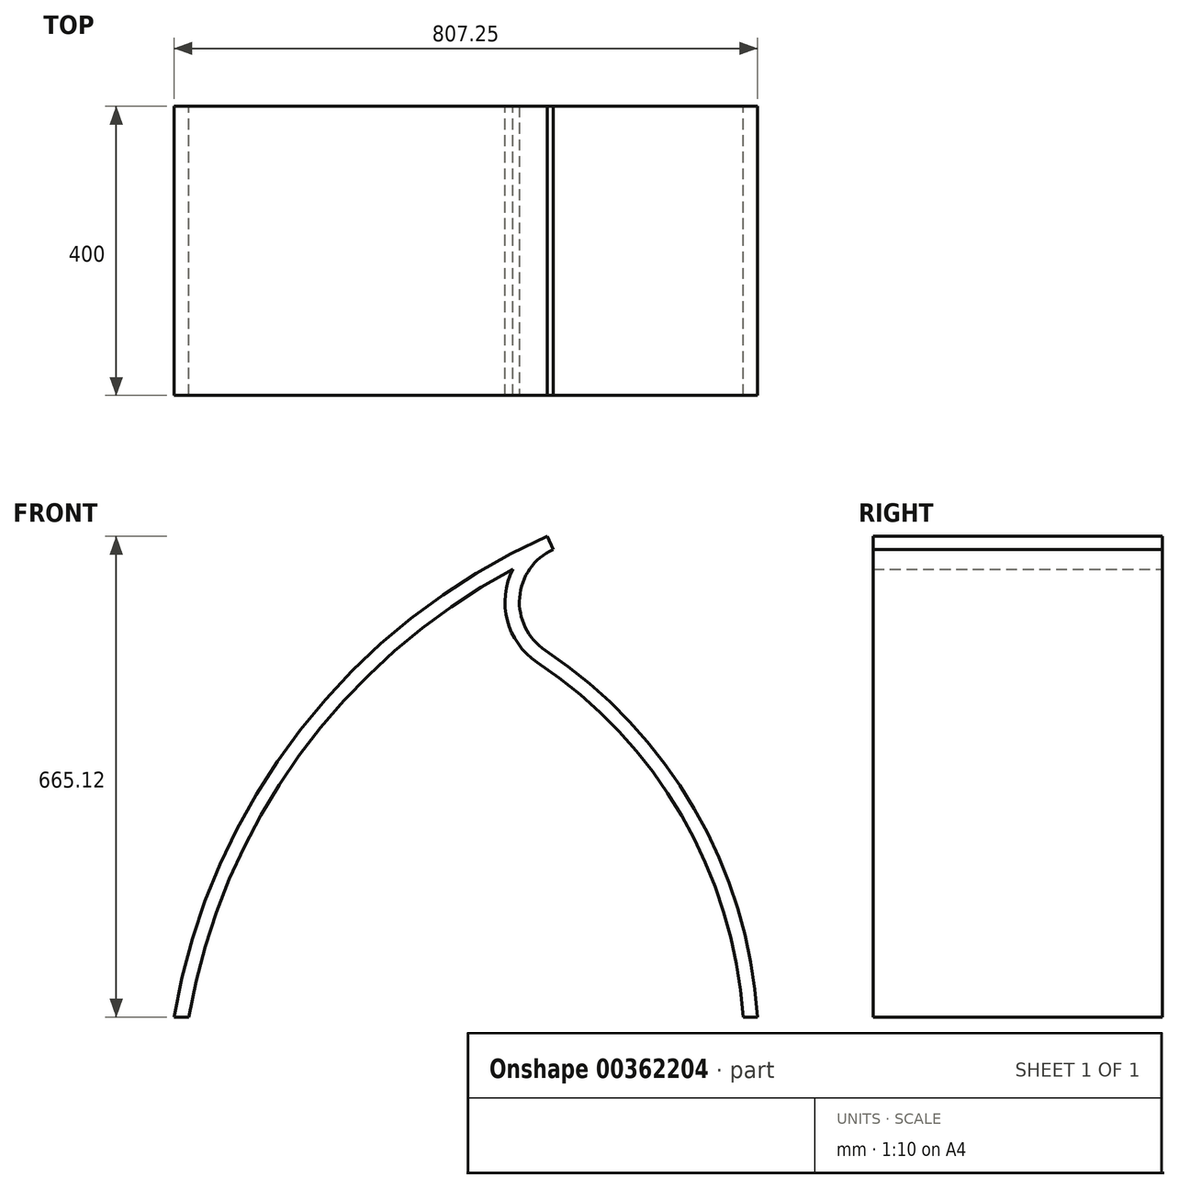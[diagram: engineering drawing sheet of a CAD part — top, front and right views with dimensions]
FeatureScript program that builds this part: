
annotation { "Feature Type Name" : "Feature", "Feature Type Description" : "" }
export const myFeature = defineFeature(function(context is Context, id is Id, definition is map)
    precondition{}
    {
        {
            var Q0;
            Q0=qCreatedBy(makeId("Front.planeOp"),FACE);
            var sketch = newSketch(context, id + "F0", { "sketchPlane" : qUnion([Q0])});
            skArc(sketch, "E0", {"start": v(516.46, 665.12) * mm, "mid": v(174.8, 397.34) * mm, "end": v(0, 0) * mm});
            skArc(sketch, "E1.0", {"start": v(524.6, 646.85) * mm, "mid": v(455.53, 612.35) * mm, "end": v(389.79, 571.88) * mm});
            skLineSegment(sketch, "E2", {"start": v(0, 0) * mm, "end": v(20.3, 0) * mm});
            skLineSegment(sketch, "E3", {"start": v(516.46, 665.12) * mm, "end": v(524.6, 646.85) * mm});
            skArc(sketch, "E4", {"start": v(807.25, 0) * mm, "mid": v(681.63, 346.61) * mm, "end": v(389.79, 571.88) * mm});
            skArc(sketch, "E5.0", {"start": v(787.2, 0) * mm, "mid": v(661.12, 340.72) * mm, "end": v(369.97, 558.03) * mm});
            skLineSegment(sketch, "E6.trimOffspring", {"start": v(787.2, 0) * mm, "end": v(807.25, 0) * mm});
            skArc(sketch, "E7", {"start": v(369.97, 558.03) * mm, "mid": v(140.43, 313.3) * mm, "end": v(20.3, 0) * mm});
            skSolve(sketch);
        }
        {
            var Q0;
            Q0 = qSketchRegion(id + "F0", true);
            extrude(context, id + "F1", {"entities" : qUnion([Q0]), "depth" : 200 * mm, "hasSecondDirection" : true, "secondDirectionOppositeDirection" : true, "secondDirectionDepth" : 200 * mm});
        }
        {
            var Q0;
            Q0=makeQuery(id+"F1.opExtrude","SWEPT_EDGE",EDGE,{"disambiguationData":[OSD([sQuery(id+"F0.wireOp",EDGE,"E1.0"),sQuery(id+"F0.wireOp",EDGE,"E4")])]});
            fillet(context, id + "F2", {"entities" : qUnion([Q0]), "radius" : 80 * mm, "tangentPropagation" : true, "allowEdgeOverflow" : false});
        }
        {
            var Q0;
            Q0=makeQuery(id+"F1.opExtrude","CAP_FACE",FACE,{"disambiguationData":[OSD([sQuery(id+"F0.wireOp",EDGE,"E0"),sQuery(id+"F0.wireOp",EDGE,"E1.0"),sQuery(id+"F0.wireOp",EDGE,"E3"),sQuery(id+"F0.wireOp",EDGE,"E4"),sQuery(id+"F0.wireOp",EDGE,"E5.0"),sQuery(id+"F0.wireOp",EDGE,"E2"),sQuery(id+"F0.wireOp",EDGE,"E6.trimOffspring"),sQuery(id+"F0.wireOp",EDGE,"E7")])],"isStart":true});
            var sketch = newSketch(context, id + "F3", { "sketchPlane" : qUnion([Q0])});
            skArc(sketch, "E8.0", {"start": v(-516.46, 665.12) * mm, "mid": v(-174.8, 397.34) * mm, "end": v(0, 0) * mm, "construction": true});
            skArc(sketch, "E9.0", {"start": v(-513.53, 507.41) * mm, "mid": v(-478.03, 580.39) * mm, "end": v(-524.6, 646.85) * mm, "construction": true});
            skArc(sketch, "E10.0", {"start": v(-502.46, 490.75) * mm, "mid": v(-438.17, 528.25) * mm, "end": v(-369.97, 558.03) * mm});
            skArc(sketch, "E11.0", {"start": v(-502.46, 490.75) * mm, "mid": v(-461.04, 548.71) * mm, "end": v(-468.72, 619.54) * mm});
            skArc(sketch, "E12.0", {"start": v(-468.72, 619.54) * mm, "mid": v(-418.32, 590.43) * mm, "end": v(-369.97, 558.03) * mm});
            skPoint(sketch, "E13.orphan", {"position": v(-787.2, 0) * mm});
            skSolve(sketch);
        }
        {
            var Q0;
            Q0 = qSketchRegion(id + "F3", true);
            extrude(context, id + "F4", {"entities" : qUnion([Q0]), "operationType" : NewBodyOperationType.REMOVE, "endBound" : BoundingType.UP_TO_NEXT, "oppositeDirection" : true, "depth" : 25 * mm});
        }
    });
